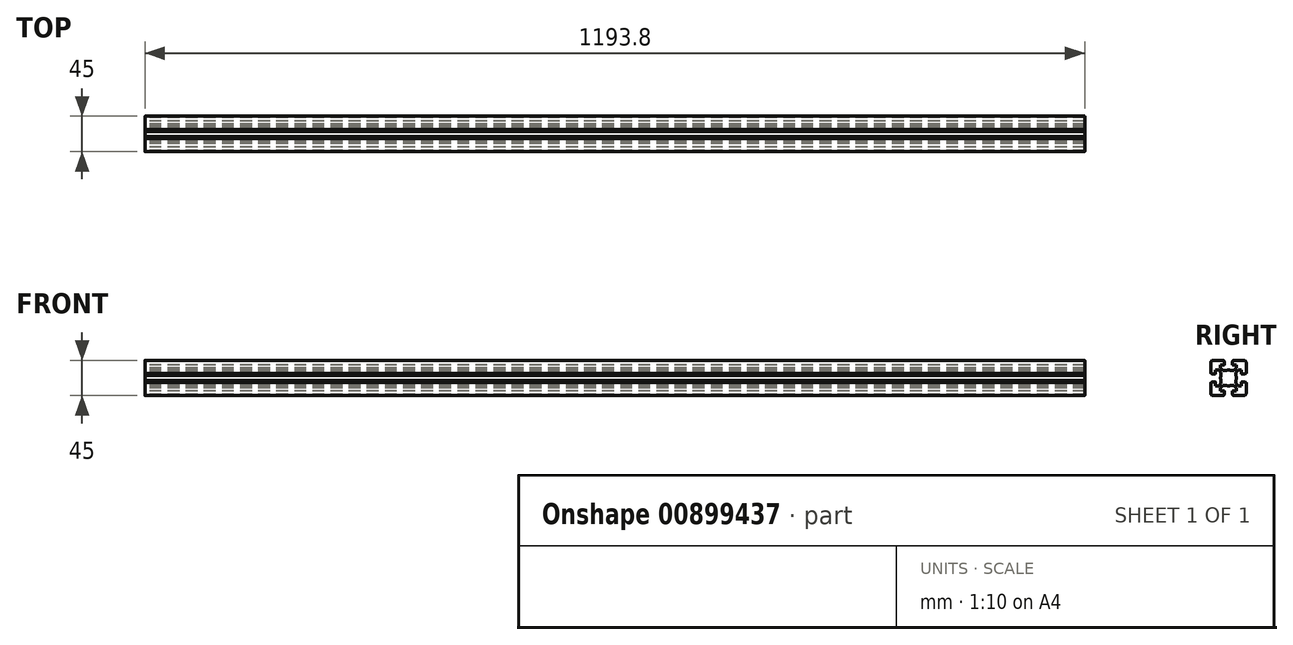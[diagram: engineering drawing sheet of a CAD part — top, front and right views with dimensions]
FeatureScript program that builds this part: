
annotation { "Feature Type Name" : "Feature", "Feature Type Description" : "" }
export const myFeature = defineFeature(function(context is Context, id is Id, definition is map)
    precondition{}
    {
        {
            var Q0;
            Q0=qCreatedBy(makeId("Right.planeOp"),FACE);
            var sketch = newSketch(context, id + "F0", { "sketchPlane" : qUnion([Q0])});
            skLineSegment(sketch, "E0", {"start": v(-20.09, -10.29) * mm, "end": v(-21.29, -10.29) * mm});
            skArc(sketch, "E1", {"start": v(-21.29, -10.29) * mm, "mid": v(-21.5, -10.38) * mm, "end": v(-21.59, -10.59) * mm});
            skLineSegment(sketch, "E2", {"start": v(-21.59, -10.59) * mm, "end": v(-21.59, -23.99) * mm});
            skArc(sketch, "E3", {"start": v(-21.59, -23.99) * mm, "mid": v(-20.7, -26.11) * mm, "end": v(-18.59, -26.99) * mm});
            skLineSegment(sketch, "E4", {"start": v(-18.59, -26.99) * mm, "end": v(-5.19, -26.99) * mm});
            skArc(sketch, "E5", {"start": v(-5.19, -26.99) * mm, "mid": v(-4.98, -26.9) * mm, "end": v(-4.89, -26.69) * mm});
            skLineSegment(sketch, "E6", {"start": v(-4.89, -26.69) * mm, "end": v(-4.89, -25.49) * mm});
            skLineSegment(sketch, "E7", {"start": v(-4.89, -25.49) * mm, "end": v(-4.39, -25.49) * mm});
            skArc(sketch, "E8", {"start": v(-4.39, -25.49) * mm, "mid": v(-4.18, -25.4) * mm, "end": v(-4.09, -25.19) * mm});
            skLineSegment(sketch, "E9", {"start": v(-4.09, -25.19) * mm, "end": v(-4.09, -21.29) * mm});
            skArc(sketch, "E10", {"start": v(-4.09, -21.29) * mm, "mid": v(-4.18, -21.08) * mm, "end": v(-4.39, -20.99) * mm});
            skLineSegment(sketch, "E11", {"start": v(-4.39, -20.99) * mm, "end": v(-9.14, -20.99) * mm});
            skLineSegment(sketch, "E12", {"start": v(-9.14, -20.99) * mm, "end": v(-9.14, -16.88) * mm});
            skLineSegment(sketch, "E13", {"start": v(-9.14, -16.88) * mm, "end": v(-6.25, -13.99) * mm});
            skLineSegment(sketch, "E14", {"start": v(-6.25, -13.99) * mm, "end": v(-2.21, -13.99) * mm});
            skArc(sketch, "E15", {"start": v(-2.21, -13.99) * mm, "mid": v(0.91, -14.49) * mm, "end": v(4.03, -13.99) * mm});
            skLineSegment(sketch, "E16", {"start": v(-20.09, -10.29) * mm, "end": v(-20.09, -9.79) * mm});
            skArc(sketch, "E17", {"start": v(-20.09, -9.79) * mm, "mid": v(-20, -9.58) * mm, "end": v(-19.79, -9.49) * mm});
            skLineSegment(sketch, "E18", {"start": v(-19.79, -9.49) * mm, "end": v(-15.89, -9.49) * mm});
            skArc(sketch, "E19", {"start": v(-15.89, -9.49) * mm, "mid": v(-15.68, -9.58) * mm, "end": v(-15.59, -9.79) * mm});
            skLineSegment(sketch, "E20", {"start": v(-15.59, -9.79) * mm, "end": v(-15.59, -14.54) * mm});
            skLineSegment(sketch, "E21", {"start": v(-15.59, -14.54) * mm, "end": v(-11.48, -14.54) * mm});
            skLineSegment(sketch, "E22", {"start": v(-11.48, -14.54) * mm, "end": v(-8.59, -11.65) * mm});
            skLineSegment(sketch, "E23", {"start": v(-8.59, -11.65) * mm, "end": v(-8.59, -7.61) * mm});
            skLineSegment(sketch, "E24", {"start": v(29.82, -4.49) * mm, "end": v(-31.05, -4.49) * mm});
            skLineSegment(sketch, "E25.MirrorCS", {"start": v(6.71, -25.49) * mm, "end": v(6.21, -25.49) * mm});
            skArc(sketch, "E26.MirrorCS", {"start": v(7.01, -26.99) * mm, "mid": v(6.8, -26.9) * mm, "end": v(6.71, -26.69) * mm});
            skLineSegment(sketch, "E27.MirrorCS", {"start": v(10.41, -11.65) * mm, "end": v(10.41, -7.61) * mm});
            skArc(sketch, "E28.MirrorCS", {"start": v(6.21, -25.49) * mm, "mid": v(6, -25.4) * mm, "end": v(5.91, -25.19) * mm});
            skLineSegment(sketch, "E29.MirrorCS", {"start": v(6.71, -26.69) * mm, "end": v(6.71, -25.49) * mm});
            skArc(sketch, "E30.MirrorCS", {"start": v(5.91, -21.29) * mm, "mid": v(6, -21.08) * mm, "end": v(6.21, -20.99) * mm});
            skLineSegment(sketch, "E31.MirrorCS", {"start": v(10.96, -16.88) * mm, "end": v(8.07, -13.99) * mm});
            skLineSegment(sketch, "E32.MirrorCS", {"start": v(13.3, -14.54) * mm, "end": v(10.41, -11.65) * mm});
            skLineSegment(sketch, "E33.MirrorCS", {"start": v(17.41, -14.54) * mm, "end": v(13.3, -14.54) * mm});
            skLineSegment(sketch, "E34.MirrorCS", {"start": v(17.41, -9.79) * mm, "end": v(17.41, -14.54) * mm});
            skLineSegment(sketch, "E35.MirrorCS", {"start": v(6.21, -20.99) * mm, "end": v(10.96, -20.99) * mm});
            skLineSegment(sketch, "E36.MirrorCS", {"start": v(8.07, -13.99) * mm, "end": v(4.03, -13.99) * mm});
            skArc(sketch, "E37.MirrorCS", {"start": v(4.03, -13.99) * mm, "mid": v(0.91, -14.49) * mm, "end": v(-2.21, -13.99) * mm});
            skLineSegment(sketch, "E38.MirrorCS", {"start": v(10.96, -20.99) * mm, "end": v(10.96, -16.88) * mm});
            skLineSegment(sketch, "E39.MirrorCS", {"start": v(5.91, -25.19) * mm, "end": v(5.91, -21.29) * mm});
            skArc(sketch, "E40.MirrorCS", {"start": v(23.41, -23.99) * mm, "mid": v(22.53, -26.11) * mm, "end": v(20.41, -26.99) * mm});
            skLineSegment(sketch, "E41.MirrorCS", {"start": v(20.41, -26.99) * mm, "end": v(7.01, -26.99) * mm});
            skLineSegment(sketch, "E42.MirrorCS", {"start": v(23.41, -10.59) * mm, "end": v(23.41, -23.99) * mm});
            skArc(sketch, "E43.MirrorCS", {"start": v(17.71, -9.49) * mm, "mid": v(17.5, -9.58) * mm, "end": v(17.41, -9.79) * mm});
            skArc(sketch, "E44.MirrorCS", {"start": v(23.11, -10.29) * mm, "mid": v(23.32, -10.38) * mm, "end": v(23.41, -10.59) * mm});
            skLineSegment(sketch, "E45.MirrorCS", {"start": v(21.91, -10.29) * mm, "end": v(21.91, -9.79) * mm});
            skLineSegment(sketch, "E46.MirrorCS", {"start": v(21.91, -10.29) * mm, "end": v(23.11, -10.29) * mm});
            skArc(sketch, "E47.MirrorCS", {"start": v(21.91, -9.79) * mm, "mid": v(21.82, -9.58) * mm, "end": v(21.61, -9.49) * mm});
            skLineSegment(sketch, "E48.MirrorCS", {"start": v(21.61, -9.49) * mm, "end": v(17.71, -9.49) * mm});
            skLineSegment(sketch, "E49.MirrorCS", {"start": v(6.71, 16.51) * mm, "end": v(6.21, 16.51) * mm});
            skArc(sketch, "E50.MirrorCS", {"start": v(-4.39, 16.51) * mm, "mid": v(-4.18, 16.42) * mm, "end": v(-4.09, 16.21) * mm});
            skLineSegment(sketch, "E51.MirrorCS", {"start": v(-4.89, 16.51) * mm, "end": v(-4.39, 16.51) * mm});
            skArc(sketch, "E52.MirrorCS", {"start": v(5.91, 12.31) * mm, "mid": v(6, 12.1) * mm, "end": v(6.21, 12.01) * mm});
            skLineSegment(sketch, "E53.MirrorCS", {"start": v(6.71, 17.71) * mm, "end": v(6.71, 16.51) * mm});
            skLineSegment(sketch, "E54.MirrorCS", {"start": v(-4.89, 17.71) * mm, "end": v(-4.89, 16.51) * mm});
            skArc(sketch, "E55.MirrorCS", {"start": v(-5.19, 18.01) * mm, "mid": v(-4.98, 17.92) * mm, "end": v(-4.89, 17.71) * mm});
            skArc(sketch, "E56.MirrorCS", {"start": v(-4.09, 12.31) * mm, "mid": v(-4.18, 12.1) * mm, "end": v(-4.39, 12.01) * mm});
            skArc(sketch, "E57.MirrorCS", {"start": v(7.01, 18.01) * mm, "mid": v(6.8, 17.92) * mm, "end": v(6.71, 17.71) * mm});
            skArc(sketch, "E58.MirrorCS", {"start": v(6.21, 16.51) * mm, "mid": v(6, 16.42) * mm, "end": v(5.91, 16.21) * mm});
            skArc(sketch, "E59.MirrorCS", {"start": v(23.11, 1.31) * mm, "mid": v(23.32, 1.4) * mm, "end": v(23.41, 1.61) * mm});
            skLineSegment(sketch, "E60.MirrorCS", {"start": v(21.91, 1.31) * mm, "end": v(21.91, 0.81) * mm});
            skArc(sketch, "E61.MirrorCS", {"start": v(-15.89, 0.51) * mm, "mid": v(-15.68, 0.6) * mm, "end": v(-15.59, 0.81) * mm});
            skArc(sketch, "E62.MirrorCS", {"start": v(-21.29, 1.31) * mm, "mid": v(-21.5, 1.4) * mm, "end": v(-21.59, 1.61) * mm});
            skArc(sketch, "E63.MirrorCS", {"start": v(17.71, 0.51) * mm, "mid": v(17.5, 0.6) * mm, "end": v(17.41, 0.81) * mm});
            skArc(sketch, "E64.MirrorCS", {"start": v(21.91, 0.81) * mm, "mid": v(21.82, 0.6) * mm, "end": v(21.61, 0.51) * mm});
            skLineSegment(sketch, "E65.MirrorCS", {"start": v(21.91, 1.31) * mm, "end": v(23.11, 1.31) * mm});
            skArc(sketch, "E66.MirrorCS", {"start": v(14.31, 5.31) * mm, "mid": v(14.1, 5.4) * mm, "end": v(14.01, 5.61) * mm});
            skArc(sketch, "E67.MirrorCS", {"start": v(-20.09, 0.81) * mm, "mid": v(-20, 0.6) * mm, "end": v(-19.79, 0.51) * mm});
            skLineSegment(sketch, "E68.MirrorCS", {"start": v(-20.09, 1.31) * mm, "end": v(-21.29, 1.31) * mm});
            skLineSegment(sketch, "E69.MirrorCS", {"start": v(-20.09, 1.31) * mm, "end": v(-20.09, 0.81) * mm});
            skLineSegment(sketch, "E70.MirrorCS", {"start": v(8.07, 5.01) * mm, "end": v(4.03, 5.01) * mm});
            skLineSegment(sketch, "E71.MirrorCS", {"start": v(-4.09, 16.21) * mm, "end": v(-4.09, 12.31) * mm});
            skLineSegment(sketch, "E72.MirrorCS", {"start": v(-9.14, 12.01) * mm, "end": v(-9.14, 7.9) * mm});
            skLineSegment(sketch, "E73.MirrorCS", {"start": v(-15.59, 5.56) * mm, "end": v(-11.48, 5.56) * mm});
            skLineSegment(sketch, "E74.MirrorCS", {"start": v(-4.39, 12.01) * mm, "end": v(-9.14, 12.01) * mm});
            skLineSegment(sketch, "E75.MirrorCS", {"start": v(-9.14, 7.9) * mm, "end": v(-6.25, 5.01) * mm});
            skLineSegment(sketch, "E76.MirrorCS", {"start": v(10.96, 12.01) * mm, "end": v(10.96, 7.9) * mm});
            skArc(sketch, "E77.MirrorCS", {"start": v(-21.59, 15.01) * mm, "mid": v(-20.7, 17.13) * mm, "end": v(-18.59, 18.01) * mm});
            skLineSegment(sketch, "E78.MirrorCS", {"start": v(23.41, 1.61) * mm, "end": v(23.41, 15.01) * mm});
            skLineSegment(sketch, "E79.MirrorCS", {"start": v(13.3, 5.56) * mm, "end": v(10.41, 2.67) * mm});
            skLineSegment(sketch, "E80.MirrorCS", {"start": v(-8.59, 2.67) * mm, "end": v(-8.59, -1.37) * mm});
            skLineSegment(sketch, "E81.MirrorCS", {"start": v(-15.59, 0.81) * mm, "end": v(-15.59, 5.56) * mm});
            skLineSegment(sketch, "E82.MirrorCS", {"start": v(10.41, 2.67) * mm, "end": v(10.41, -1.37) * mm});
            skLineSegment(sketch, "E83.MirrorCS", {"start": v(-18.59, 18.01) * mm, "end": v(-5.19, 18.01) * mm});
            skLineSegment(sketch, "E84.MirrorCS", {"start": v(10.96, 7.9) * mm, "end": v(8.07, 5.01) * mm});
            skLineSegment(sketch, "E85.MirrorCS", {"start": v(17.41, 5.56) * mm, "end": v(13.3, 5.56) * mm});
            skArc(sketch, "E86.MirrorCS", {"start": v(23.41, 15.01) * mm, "mid": v(22.53, 17.13) * mm, "end": v(20.41, 18.01) * mm});
            skLineSegment(sketch, "E87.MirrorCS", {"start": v(5.91, 16.21) * mm, "end": v(5.91, 12.31) * mm});
            skLineSegment(sketch, "E88.MirrorCS", {"start": v(17.41, 0.81) * mm, "end": v(17.41, 5.56) * mm});
            skLineSegment(sketch, "E89.MirrorCS", {"start": v(-11.48, 5.56) * mm, "end": v(-8.59, 2.67) * mm});
            skLineSegment(sketch, "E90.MirrorCS", {"start": v(-6.25, 5.01) * mm, "end": v(-2.21, 5.01) * mm});
            skLineSegment(sketch, "E91.MirrorCS", {"start": v(-21.59, 1.61) * mm, "end": v(-21.59, 15.01) * mm});
            skArc(sketch, "E92.MirrorCS", {"start": v(4.03, 5.01) * mm, "mid": v(0.91, 5.51) * mm, "end": v(-2.21, 5.01) * mm});
            skLineSegment(sketch, "E93.MirrorCS", {"start": v(6.21, 12.01) * mm, "end": v(10.96, 12.01) * mm});
            skArc(sketch, "E94.MirrorCS", {"start": v(-2.21, 5.01) * mm, "mid": v(0.91, 5.51) * mm, "end": v(4.03, 5.01) * mm});
            skLineSegment(sketch, "E95.MirrorCS", {"start": v(20.41, 18.01) * mm, "end": v(7.01, 18.01) * mm});
            skLineSegment(sketch, "E96.MirrorCS", {"start": v(-19.79, 0.51) * mm, "end": v(-15.89, 0.51) * mm});
            skLineSegment(sketch, "E97.MirrorCS", {"start": v(21.61, 0.51) * mm, "end": v(17.71, 0.51) * mm});
            skLineSegment(sketch, "E98.MirrorCS", {"start": v(0.91, -27.65) * mm, "end": v(0.91, 19.82) * mm});
            skArc(sketch, "E99", {"start": v(-8.59, -1.37) * mm, "mid": v(-9.09, -4.49) * mm, "end": v(-8.59, -7.61) * mm});
            skArc(sketch, "E100", {"start": v(10.41, -7.61) * mm, "mid": v(10.91, -4.49) * mm, "end": v(10.41, -1.37) * mm});
            skSolve(sketch);
        }
        {
            var Q0;
            Q0=qSketchRegion(id+"F0",true);
            extrude(context, id + "F1", {"entities" : qUnion([Q0]), "depth" : 1193.8 * mm, "offsetDistance" : 25.4 * mm});
        }
    });
